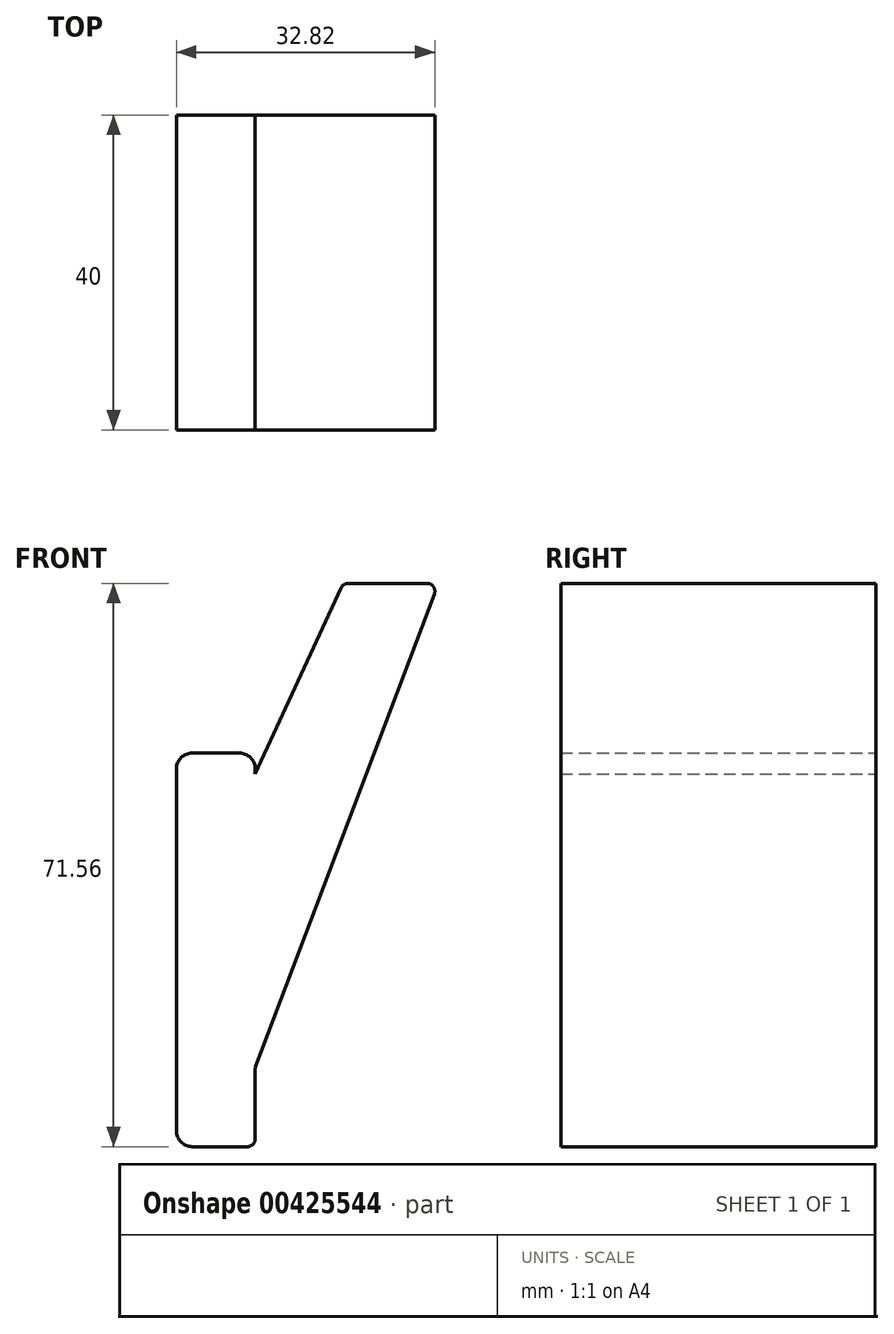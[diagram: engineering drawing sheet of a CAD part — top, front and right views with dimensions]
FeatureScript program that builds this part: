
annotation { "Feature Type Name" : "Feature", "Feature Type Description" : "" }
export const myFeature = defineFeature(function(context is Context, id is Id, definition is map)
    precondition{}
    {
        {
            var Q0;
            Q0=qCreatedBy(makeId("Front.planeOp"),FACE);
            var sketch = newSketch(context, id + "F0", { "sketchPlane" : qUnion([Q0])});
            skLineSegment(sketch, "E0", {"start": v(-10, 2) * mm, "end": v(-10, 48) * mm});
            skLineSegment(sketch, "E1", {"start": v(-8, 50) * mm, "end": v(-2, 50) * mm});
            skLineSegment(sketch, "E2", {"start": v(0, 48) * mm, "end": v(0, 47.32) * mm});
            skPoint(sketch, "E3.visualSharp", {"position": v(0, 50) * mm});
            skArc(sketch, "E3.filletArc", {"start": v(0, 48) * mm, "mid": v(-0.59, 49.41) * mm, "end": v(-2, 50) * mm});
            skPoint(sketch, "E4.visualSharp", {"position": v(-10, 50) * mm});
            skArc(sketch, "E4.filletArc", {"start": v(-8, 50) * mm, "mid": v(-9.41, 49.41) * mm, "end": v(-10, 48) * mm});
            skPoint(sketch, "E5.visualSharp", {"position": v(-10, 0) * mm});
            skArc(sketch, "E5.filletArc", {"start": v(-10, 2) * mm, "mid": v(-9.41, 0.59) * mm, "end": v(-8, 0) * mm});
            skPoint(sketch, "E6.visualSharp", {"position": v(0, 0) * mm});
            skLineSegment(sketch, "E7", {"start": v(-8, 0) * mm, "end": v(-1, 0) * mm});
            skLineSegment(sketch, "E8", {"start": v(0, 1) * mm, "end": v(0, 9.82) * mm});
            skLineSegment(sketch, "E9", {"start": v(0.06, 10.17) * mm, "end": v(22.75, 70.2) * mm});
            skLineSegment(sketch, "E10", {"start": v(21.82, 71.56) * mm, "end": v(11.82, 71.56) * mm});
            skLineSegment(sketch, "E11", {"start": v(10.91, 70.98) * mm, "end": v(0, 47.32) * mm});
            skPoint(sketch, "E12.visualSharp", {"position": v(11.18, 71.56) * mm});
            skArc(sketch, "E12.filletArc", {"start": v(11.82, 71.56) * mm, "mid": v(11.28, 71.4) * mm, "end": v(10.91, 70.98) * mm});
            skPoint(sketch, "E13.visualSharp", {"position": v(23.27, 71.56) * mm});
            skArc(sketch, "E13.filletArc", {"start": v(22.75, 70.2) * mm, "mid": v(22.64, 71.13) * mm, "end": v(21.82, 71.56) * mm});
            skPoint(sketch, "E14.visualSharp", {"position": v(0, 10) * mm});
            skArc(sketch, "E14.filletArc", {"start": v(0.06, 10.17) * mm, "mid": v(0.02, 10) * mm, "end": v(0, 9.82) * mm});
            skArc(sketch, "E15.filletArc", {"start": v(-1, 0) * mm, "mid": v(-0.3, 0.3) * mm, "end": v(0, 1) * mm});
            skSolve(sketch);
        }
        {
            var Q0;
            Q0=makeQuery(id+"F0.imprint","IMPRINT",FACE,{"disambiguationData":[TD([[makeQuery(id+"F0.imprint","IMPRINT",EDGE,{"derivedFrom":sQuery(id+"F0.wireOp",EDGE,"E0")}),-1.0]])]});
            extrude(context, id + "F1", {"entities" : qUnion([Q0]), "depth" : 40 * mm});
        }
    });
